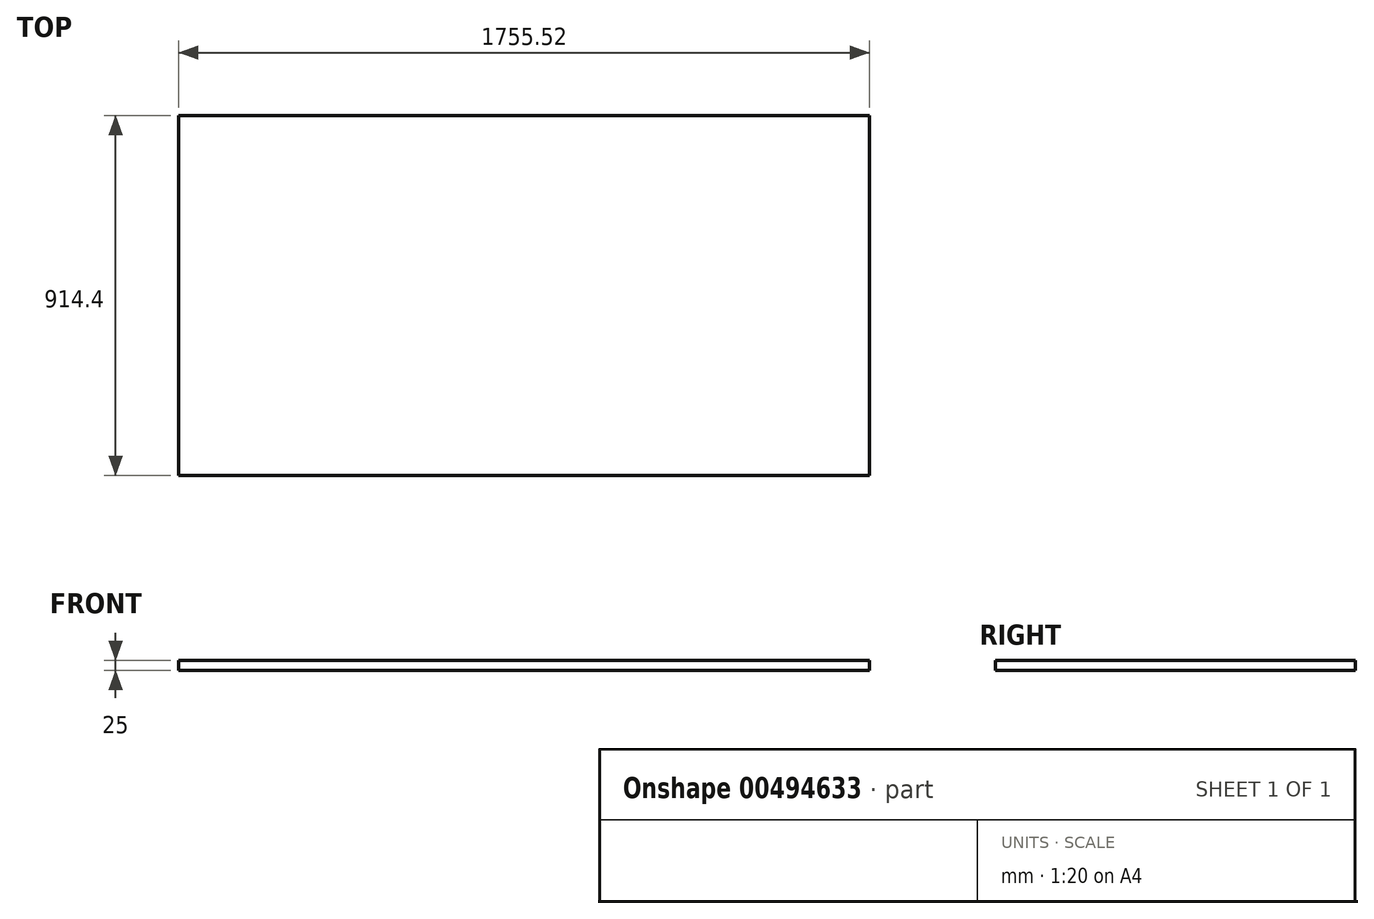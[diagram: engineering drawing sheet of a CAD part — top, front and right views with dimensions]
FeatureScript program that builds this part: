
annotation { "Feature Type Name" : "Feature", "Feature Type Description" : "" }
export const myFeature = defineFeature(function(context is Context, id is Id, definition is map)
    precondition{}
    {
        {
            var Q0;
            Q0=qCreatedBy(makeId("Top.planeOp"),FACE);
            var sketch = newSketch(context, id + "F0", { "sketchPlane" : qUnion([Q0])});
            skLineSegment(sketch, "E0.bottom", {"start": v(-1755.52, 914.4) * mm, "end": v(0, 914.4) * mm});
            skLineSegment(sketch, "E0.top", {"start": v(-1755.52, 0) * mm, "end": v(0, 0) * mm});
            skLineSegment(sketch, "E0.left", {"start": v(-1755.52, 914.4) * mm, "end": v(-1755.52, 0) * mm});
            skLineSegment(sketch, "E0.right", {"start": v(0, 914.4) * mm, "end": v(0, 0) * mm});
            skSolve(sketch);
        }
        {
            var Q0;
            Q0 = qSketchRegion(id + "F0", true);
            extrude(context, id + "F1", {"entities" : qUnion([Q0]), "depth" : 25 * mm});
        }
    });
